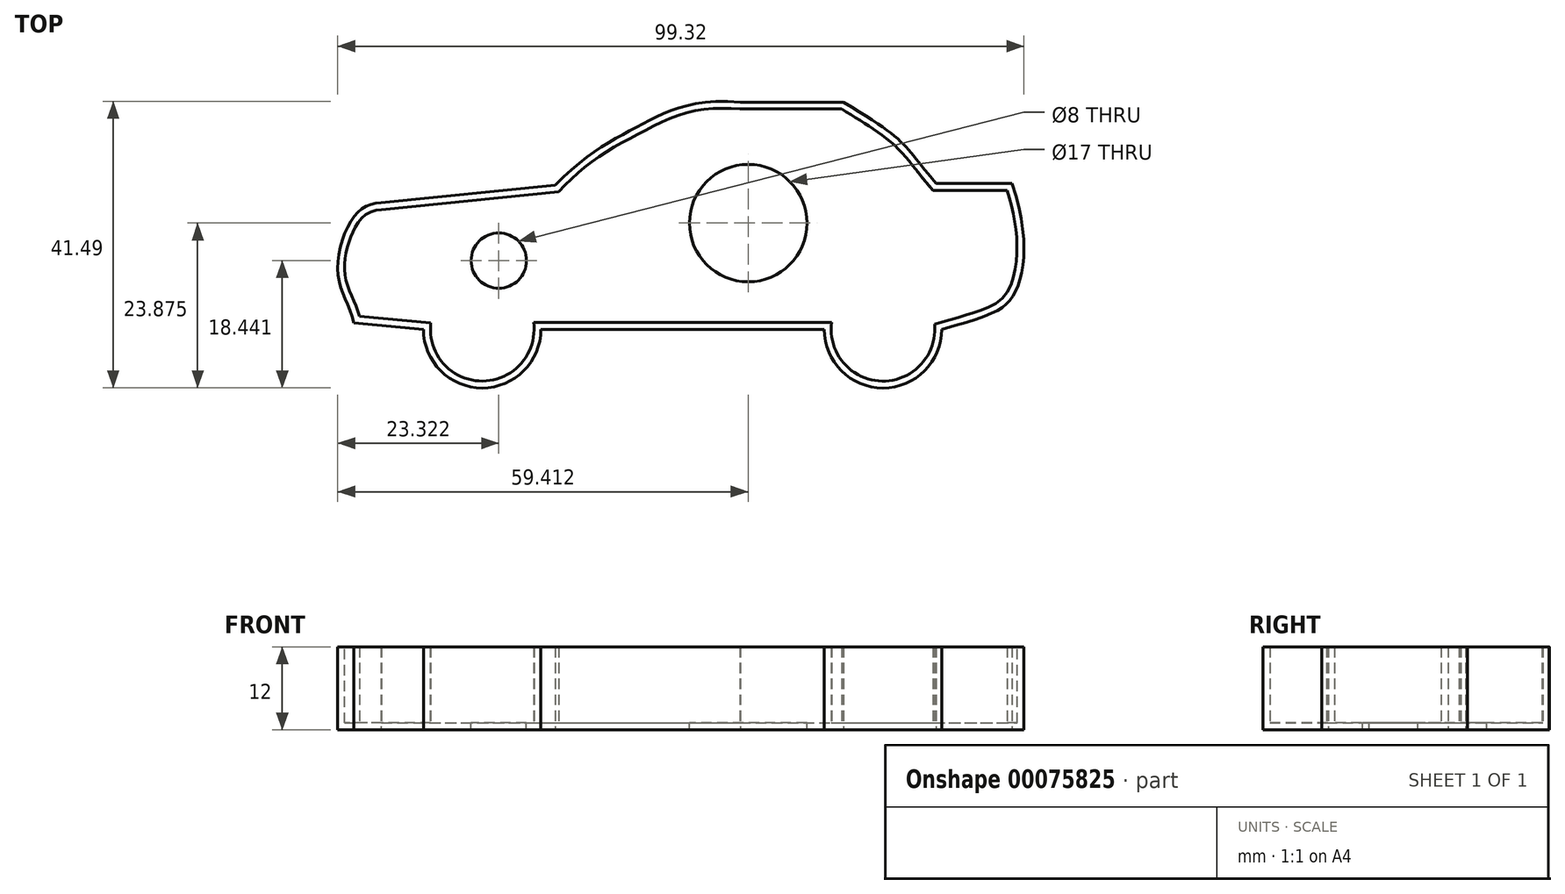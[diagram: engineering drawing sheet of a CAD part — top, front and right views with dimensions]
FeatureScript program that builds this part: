
annotation { "Feature Type Name" : "Feature", "Feature Type Description" : "" }
export const myFeature = defineFeature(function(context is Context, id is Id, definition is map)
    precondition{}
    {
        {
            var Q0;
            Q0=qCreatedBy(makeId("Top.planeOp"),FACE);
            var sketch = newSketch(context, id + "F0", { "sketchPlane" : qUnion([Q0])});
            skLineSegment(sketch, "E0", {"start": v(-50.8, 37.8) * mm, "end": v(49.2, 37.8) * mm, "construction": true});
            skLineSegment(sketch, "E1", {"start": v(-50.8, 37.8) * mm, "end": v(-50.8, -22.2) * mm, "construction": true});
            skLineSegment(sketch, "E2", {"start": v(49.2, 37.8) * mm, "end": v(49.2, -22.2) * mm, "construction": true});
            skSolve(sketch);
        }
        {
            var Q0;
            Q0=qCreatedBy(makeId("Top.planeOp"),FACE);
            var sketch = newSketch(context, id + "F1", { "sketchPlane" : qUnion([Q0])});
            skLineSegment(sketch, "E3", {"start": v(-21.45, -5.25) * mm, "end": v(19.55, -5.25) * mm});
            skLineSegment(sketch, "E4", {"start": v(-38.45, -5.25) * mm, "end": v(-48.5, -4.3) * mm});
            skLineSegment(sketch, "E5", {"start": v(-44.57, 13.05) * mm, "end": v(-19.36, 15.62) * mm});
            skLineSegment(sketch, "E6", {"start": v(7.39, 27.65) * mm, "end": v(22.36, 27.65) * mm});
            skLineSegment(sketch, "E7", {"start": v(35.73, 15.87) * mm, "end": v(46.71, 15.87) * mm});
            skFitSpline(sketch, "E8", {"points": [v(-19.36, 15.62) * mm, v(-7.19, 24.24) * mm, v(7.39, 27.65) * mm], "startDerivative": vector(27.28, 28.64) * mm, "endDerivative": vector(44.28, -3.4) * mm});
            skFitSpline(sketch, "E9", {"points": [v(36.55, -5.25) * mm, v(47.11, 0) * mm, v(46.71, 15.87) * mm], "startDerivative": vector(46.65, 13.11) * mm, "endDerivative": vector(-14.28, 41.7) * mm});
            skFitSpline(sketch, "E10", {"points": [v(-44.57, 13.05) * mm, v(-48.71, 10.81) * mm, v(-50.8, 2.5) * mm, v(-48.5, -4.3) * mm], "startDerivative": vector(-18.76, 0) * mm, "endDerivative": vector(5.22, -22.61) * mm});
            skFitSpline(sketch, "E11", {"points": [v(22.36, 27.65) * mm, v(35.73, 15.87) * mm], "startDerivative": vector(28.75, -17.42) * mm, "endDerivative": vector(14.61, -17.24) * mm});
            skArc(sketch, "E12", {"start": v(19.55, -5.25) * mm, "mid": v(28.05, -13.75) * mm, "end": v(36.55, -5.25) * mm});
            skArc(sketch, "E13", {"start": v(-38.45, -5.25) * mm, "mid": v(-29.95, -13.75) * mm, "end": v(-21.45, -5.25) * mm});
            skSolve(sketch);
        }
        {
            var Q0;
            Q0=makeQuery(id+"F1.imprint","IMPRINT",FACE,{"disambiguationData":[TD([[makeQuery(id+"F1.imprint","IMPRINT",EDGE,{"derivedFrom":sQuery(id+"F1.wireOp",EDGE,"E3")}),1.0]])]});
            extrude(context, id + "F2", {"entities" : qUnion([Q0]), "depth" : 12 * mm});
        }
        {
            var Q0;
            Q0=makeQuery(id+"F2.opExtrude","CAP_FACE",FACE,{"disambiguationData":[OSD([sQuery(id+"F1.wireOp",EDGE,"E3"),sQuery(id+"F1.wireOp",EDGE,"E4"),sQuery(id+"F1.wireOp",EDGE,"E5"),sQuery(id+"F1.wireOp",EDGE,"E6"),sQuery(id+"F1.wireOp",EDGE,"E7"),sQuery(id+"F1.wireOp",EDGE,"E8"),sQuery(id+"F1.wireOp",EDGE,"7ad47381-5203-4c9c-b62b-c72e9e109743"),sQuery(id+"F1.wireOp",EDGE,"E9"),sQuery(id+"F1.wireOp",EDGE,"E10"),sQuery(id+"F1.wireOp",EDGE,"75635c7e-1656-4f71-a0cf-f363c605da60"),sQuery(id+"F1.wireOp",EDGE,"E11")])],"isStart":false});
            shell(context, id + "F3", {"entities" : qUnion([Q0]), "thickness" : 1 * mm});
        }
        {
            var Q0;
            Q0=makeQuery(id+"F3.opShell","OFFSET_FACE",FACE,{"disambiguationData":[OSD([sQuery(id+"F1.wireOp",EDGE,"E3"),sQuery(id+"F1.wireOp",EDGE,"E4"),sQuery(id+"F1.wireOp",EDGE,"E5"),sQuery(id+"F1.wireOp",EDGE,"E6"),sQuery(id+"F1.wireOp",EDGE,"E7"),sQuery(id+"F1.wireOp",EDGE,"E8"),sQuery(id+"F1.wireOp",EDGE,"7ad47381-5203-4c9c-b62b-c72e9e109743"),sQuery(id+"F1.wireOp",EDGE,"E9"),sQuery(id+"F1.wireOp",EDGE,"E10"),sQuery(id+"F1.wireOp",EDGE,"75635c7e-1656-4f71-a0cf-f363c605da60"),sQuery(id+"F1.wireOp",EDGE,"E11")])]});
            var sketch = newSketch(context, id + "F4", { "sketchPlane" : qUnion([Q0])});
            skCircle(sketch, "E14", {"center": v(8.54, 10.12) * mm, "radius": 8.5 * mm});
            skCircle(sketch, "E15", {"center": v(-27.55, 4.7) * mm, "radius": 4 * mm});
            skSolve(sketch);
        }
        {
            var Q0;
            Q0 = qSketchRegion(id + "F4", true);
            extrude(context, id + "F5", {"entities" : qUnion([Q0]), "operationType" : NewBodyOperationType.REMOVE, "oppositeDirection" : true, "depth" : 25 * mm});
        }
    });
